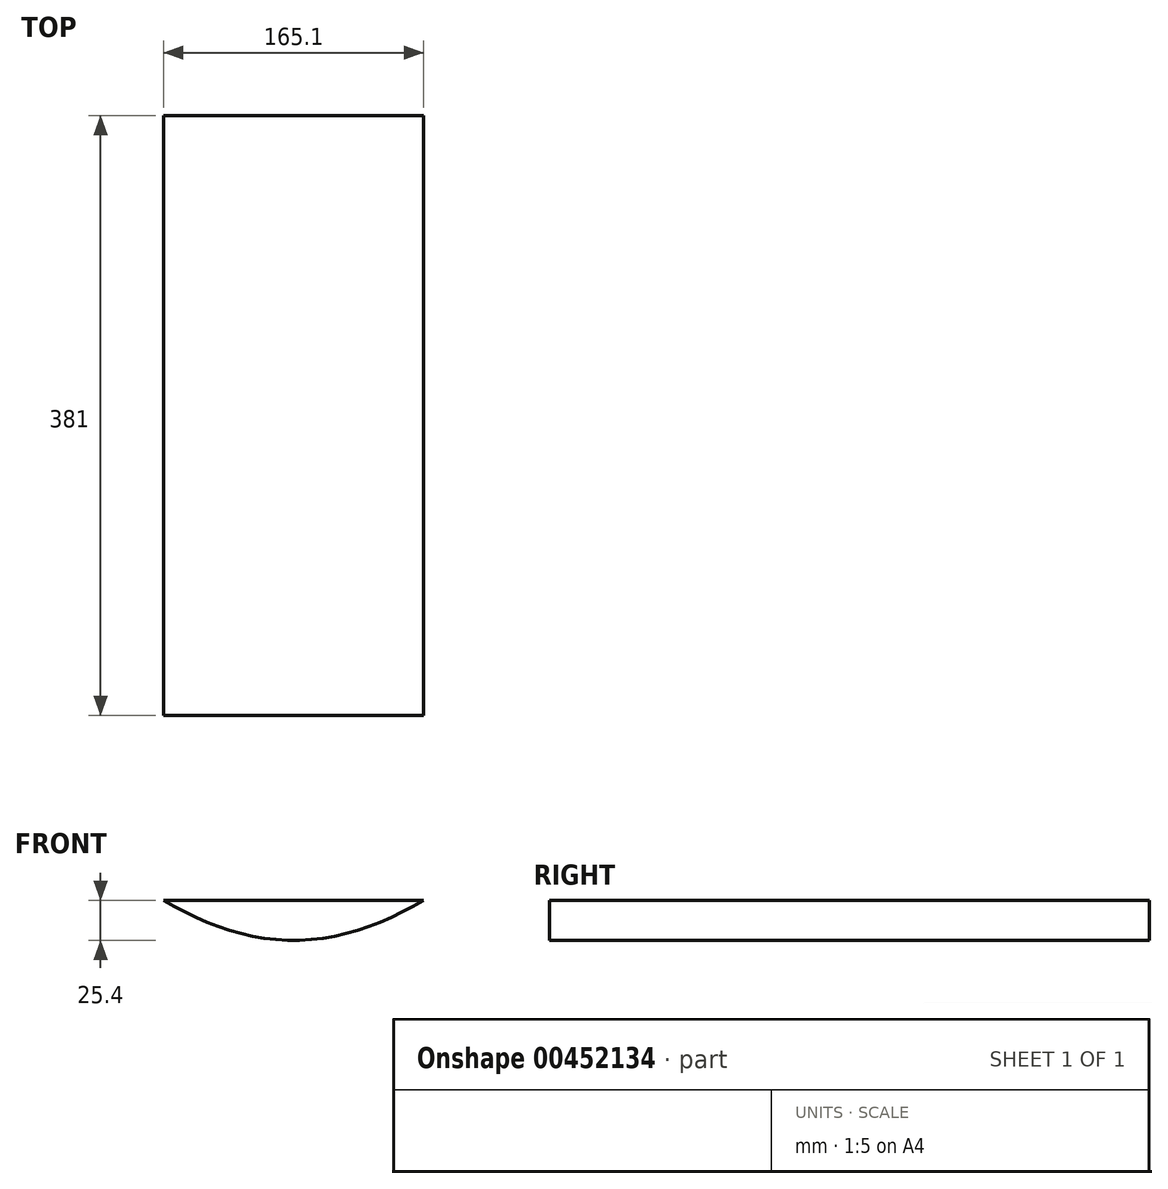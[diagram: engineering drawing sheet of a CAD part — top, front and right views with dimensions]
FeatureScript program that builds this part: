
annotation { "Feature Type Name" : "Feature", "Feature Type Description" : "" }
export const myFeature = defineFeature(function(context is Context, id is Id, definition is map)
    precondition{}
    {
        {
            var Q0;
            Q0=qCreatedBy(makeId("Front.planeOp"),FACE);
            var sketch = newSketch(context, id + "F0", { "sketchPlane" : qUnion([Q0])});
            skFitSpline(sketch, "E0", {"points": [v(0, 0) * mm, v(-82.55, -25.4) * mm, v(-165.1, 0) * mm], "startDerivative": vector(-152.4, -91.44) * mm, "endDerivative": vector(-152.4, 91.44) * mm});
            skLineSegment(sketch, "E1", {"start": v(-165.1, 0) * mm, "end": v(0, 0) * mm});
            skSolve(sketch);
        }
        {
            var Q0;
            Q0=qCreatedBy(makeId("Front.planeOp"),FACE);
            cPlane(context, id + "F1", {"entities" : qUnion([Q0]), "cplaneType" : CPlaneType.OFFSET, "offset" : 381 * mm, "oppositeDirection" : true, "width" : 152.4 * mm, "height" : 152.4 * mm});
        }
        {
            var Q0;
            Q0=qCreatedBy(id+"F1.planeOp",FACE);
            var sketch = newSketch(context, id + "F2", { "sketchPlane" : qUnion([Q0])});
            skLineSegment(sketch, "E2.0", {"start": v(-165.1, 0) * mm, "end": v(0, 0) * mm});
            skPoint(sketch, "E3", {"position": v(-82.55, 0) * mm});
            skSolve(sketch);
        }
        {
            var Q0;
            Q0=sQuery(id+"F0.wireOp",EDGE,"E0");
            cPoint(context, id + "F3", {"entities" : qUnion([Q0]), "parameter" : 0.5});
        }
        {
            var Q0;
            Q0=qCreatedBy(makeId("Right.planeOp"),FACE);
            var Q1;
            Q1 = qCreatedBy(id + "F3" ,VERTEX);
            cPlane(context, id + "F4", {"entities" : qUnion([Q0, Q1]), "cplaneType" : CPlaneType.PLANE_POINT, "offset" : 25.4 * mm, "width" : 152.4 * mm, "height" : 152.4 * mm});
        }
        {
            var Q0;
            Q0=makeQuery(id+"F0.imprint","IMPRINT",FACE,{"disambiguationData":[TD([[makeQuery(id+"F0.imprint","IMPRINT",EDGE,{"derivedFrom":sQuery(id+"F0.wireOp",EDGE,"E0")}),-1.0]])]});
            var Q1;
            Q1=sQuery(id+"F0.wireOp",EDGE,"E0");
            var Q2;
            Q2=sQuery(id+"F0.wireOp",EDGE,"E1");
            var Q3;
            Q3=sQuery(id+"F2.wireOp",VERTEX,"E3");
            extrude(context, id + "F5", {"entities" : qUnion([Q0]), "surfaceEntities" : qUnion([Q1, Q2]), "endBound" : BoundingType.UP_TO_VERTEX, "oppositeDirection" : true, "endBoundEntityVertex" : qUnion([Q3]), "depth" : 25.4 * mm});
        }
    });
